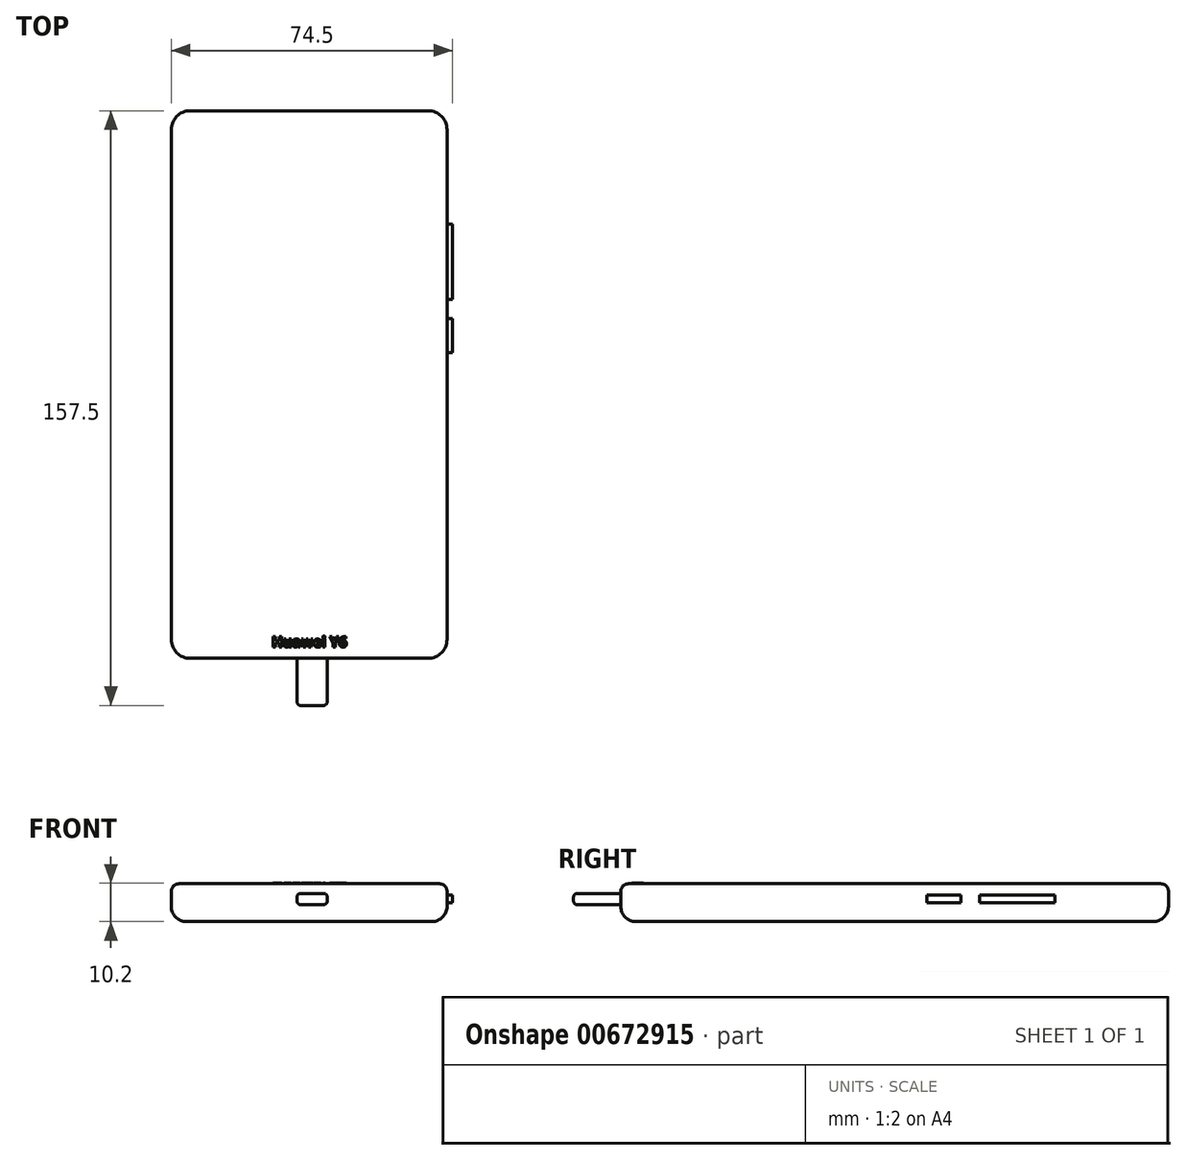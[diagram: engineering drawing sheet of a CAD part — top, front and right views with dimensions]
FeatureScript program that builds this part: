
annotation { "Feature Type Name" : "Feature", "Feature Type Description" : "" }
export const myFeature = defineFeature(function(context is Context, id is Id, definition is map)
    precondition{}
    {
        {
            var Q0;
            Q0=qCreatedBy(makeId("Top.planeOp"),FACE);
            var sketch = newSketch(context, id + "F0", { "sketchPlane" : qUnion([Q0])});
            skLineSegment(sketch, "E0.bottom", {"start": v(31.5, -72.5) * mm, "end": v(-31.5, -72.5) * mm});
            skLineSegment(sketch, "E0.top", {"start": v(31.5, 72.5) * mm, "end": v(-31.5, 72.5) * mm});
            skLineSegment(sketch, "E0.left", {"start": v(36.5, -67.5) * mm, "end": v(36.5, 67.5) * mm});
            skLineSegment(sketch, "E0.right", {"start": v(-36.5, -67.5) * mm, "end": v(-36.5, 67.5) * mm});
            skPoint(sketch, "E0.middle", {"position": v(0, 0) * mm});
            skPoint(sketch, "E1.visualSharp", {"position": v(-36.5, 72.5) * mm});
            skArc(sketch, "E1.filletArc", {"start": v(-31.5, 72.5) * mm, "mid": v(-35.04, 71.04) * mm, "end": v(-36.5, 67.5) * mm});
            skPoint(sketch, "E2.visualSharp", {"position": v(36.5, 72.5) * mm});
            skArc(sketch, "E2.filletArc", {"start": v(36.5, 67.5) * mm, "mid": v(35.04, 71.04) * mm, "end": v(31.5, 72.5) * mm});
            skPoint(sketch, "E3.visualSharp", {"position": v(36.5, -72.5) * mm});
            skArc(sketch, "E3.filletArc", {"start": v(31.5, -72.5) * mm, "mid": v(35.04, -71.04) * mm, "end": v(36.5, -67.5) * mm});
            skPoint(sketch, "E4.visualSharp", {"position": v(-36.5, -72.5) * mm});
            skArc(sketch, "E4.filletArc", {"start": v(-36.5, -67.5) * mm, "mid": v(-35.04, -71.04) * mm, "end": v(-31.5, -72.5) * mm});
            skSolve(sketch);
        }
        {
            var Q0;
            Q0 = qSketchRegion(id + "F0", true);
            extrude(context, id + "F1", {"entities" : qUnion([Q0]), "depth" : 10 * mm, "offsetDistance" : 25 * mm});
        }
        {
            var Q0;
            Q0=makeQuery(id+"F1.opExtrude","CAP_EDGE",EDGE,{"disambiguationData":[OSD([sQuery(id+"F0.wireOp",EDGE,"E1.filletArc")])],"isStart":false});
            fillet(context, id + "F2", {"entities" : qUnion([Q0]), "radius" : 2 * mm, "tangentPropagation" : true, "allowEdgeOverflow" : false});
        }
        {
            var Q0;
            Q0=makeQuery(id+"F1.opExtrude","CAP_EDGE",EDGE,{"disambiguationData":[OSD([sQuery(id+"F0.wireOp",EDGE,"E1.filletArc")])],"isStart":true});
            fillet(context, id + "F3", {"entities" : qUnion([Q0]), "radius" : 4 * mm, "tangentPropagation" : true, "allowEdgeOverflow" : false});
        }
        {
            var Q0;
            Q0=qCreatedBy(makeId("Right.planeOp"),FACE);
            var sketch = newSketch(context, id + "F4", { "sketchPlane" : qUnion([Q0])});
            skLineSegment(sketch, "E5.bottom", {"start": v(42.5, 7) * mm, "end": v(22.5, 7) * mm});
            skLineSegment(sketch, "E5.top", {"start": v(42.5, 5) * mm, "end": v(22.5, 5) * mm});
            skLineSegment(sketch, "E5.left", {"start": v(42.5, 7) * mm, "end": v(42.5, 5) * mm});
            skLineSegment(sketch, "E5.right", {"start": v(22.5, 7) * mm, "end": v(22.5, 5) * mm});
            skSolve(sketch);
        }
        {
            var Q0;
            Q0 = qSketchRegion(id + "F4", true);
            extrude(context, id + "F5", {"entities" : qUnion([Q0]), "operationType" : NewBodyOperationType.ADD, "depth" : 38 * mm, "offsetDistance" : 25 * mm});
        }
        {
            var Q0;
            Q0=qCreatedBy(makeId("Right.planeOp"),FACE);
            var sketch = newSketch(context, id + "F6", { "sketchPlane" : qUnion([Q0])});
            skLineSegment(sketch, "E6.bottom", {"start": v(8.5, 7) * mm, "end": v(17.5, 7) * mm});
            skLineSegment(sketch, "E6.top", {"start": v(8.5, 5) * mm, "end": v(17.5, 5) * mm});
            skLineSegment(sketch, "E6.left", {"start": v(8.5, 7) * mm, "end": v(8.5, 5) * mm});
            skLineSegment(sketch, "E6.right", {"start": v(17.5, 7) * mm, "end": v(17.5, 5) * mm});
            skSolve(sketch);
        }
        {
            var Q0;
            Q0 = qSketchRegion(id + "F6", true);
            extrude(context, id + "F7", {"entities" : qUnion([Q0]), "operationType" : NewBodyOperationType.ADD, "depth" : 38 * mm, "offsetDistance" : 25 * mm});
        }
        {
            var Q0;
            Q0=qCreatedBy(makeId("Front.planeOp"),FACE);
            var sketch = newSketch(context, id + "F8", { "sketchPlane" : qUnion([Q0])});
            skLineSegment(sketch, "E7.bottom", {"start": v(-3.21, 7.45) * mm, "end": v(4.79, 7.45) * mm});
            skLineSegment(sketch, "E7.top", {"start": v(-3.21, 4.45) * mm, "end": v(4.79, 4.45) * mm});
            skLineSegment(sketch, "E7.left", {"start": v(-3.21, 7.45) * mm, "end": v(-3.21, 4.45) * mm});
            skLineSegment(sketch, "E7.right", {"start": v(4.79, 7.45) * mm, "end": v(4.79, 4.45) * mm});
            skSolve(sketch);
        }
        {
            var Q0;
            Q0 = qSketchRegion(id + "F8", true);
            extrude(context, id + "F9", {"entities" : qUnion([Q0]), "operationType" : NewBodyOperationType.ADD, "depth" : 85 * mm, "offsetDistance" : 25 * mm});
        }
        {
            var Q0;
            Q0=makeQuery(id+"F9.opExtrude","SWEPT_EDGE",EDGE,{"disambiguationData":[OSD([sQuery(id+"F8.wireOp",EDGE,"E7.bottom"),sQuery(id+"F8.wireOp",EDGE,"E7.right")])]});
            var Q1;
            Q1=makeQuery(id+"F9.opExtrude","CAP_EDGE",EDGE,{"disambiguationData":[OSD([sQuery(id+"F8.wireOp",EDGE,"E7.bottom")])],"isStart":false});
            var Q2;
            Q2=makeQuery(id+"F9.opExtrude","SWEPT_EDGE",EDGE,{"disambiguationData":[OSD([sQuery(id+"F8.wireOp",EDGE,"E7.bottom"),sQuery(id+"F8.wireOp",EDGE,"E7.left")])]});
            var Q3;
            Q3=makeQuery(id+"F9.opExtrude","CAP_EDGE",EDGE,{"disambiguationData":[OSD([sQuery(id+"F8.wireOp",EDGE,"E7.left")])],"isStart":false});
            var Q4;
            Q4=makeQuery(id+"F9.opExtrude","SWEPT_EDGE",EDGE,{"disambiguationData":[OSD([sQuery(id+"F8.wireOp",EDGE,"E7.top"),sQuery(id+"F8.wireOp",EDGE,"E7.left")])]});
            var Q5;
            Q5=makeQuery(id+"F9.opExtrude","CAP_EDGE",EDGE,{"disambiguationData":[OSD([sQuery(id+"F8.wireOp",EDGE,"E7.top")])],"isStart":false});
            var Q6;
            Q6=makeQuery(id+"F9.opExtrude","SWEPT_EDGE",EDGE,{"disambiguationData":[OSD([sQuery(id+"F8.wireOp",EDGE,"E7.top"),sQuery(id+"F8.wireOp",EDGE,"E7.right")])]});
            var Q7;
            Q7=makeQuery(id+"F9.opExtrude","CAP_EDGE",EDGE,{"disambiguationData":[OSD([sQuery(id+"F8.wireOp",EDGE,"E7.right")])],"isStart":false});
            fillet(context, id + "F10", {"entities" : qUnion([Q0, Q1, Q2, Q3, Q4, Q5, Q6, Q7]), "radius" : 1 * mm, "tangentPropagation" : true, "allowEdgeOverflow" : false});
        }
        {
            var Q0;
            Q0=makeQuery(id+"F1.opExtrude","CAP_FACE",FACE,{"disambiguationData":[OSD([sQuery(id+"F0.wireOp",EDGE,"E0.bottom"),sQuery(id+"F0.wireOp",EDGE,"E0.top"),sQuery(id+"F0.wireOp",EDGE,"E0.left"),sQuery(id+"F0.wireOp",EDGE,"E0.right"),sQuery(id+"F0.wireOp",EDGE,"E1.filletArc"),sQuery(id+"F0.wireOp",EDGE,"E2.filletArc"),sQuery(id+"F0.wireOp",EDGE,"E3.filletArc"),sQuery(id+"F0.wireOp",EDGE,"E4.filletArc")])],"isStart":false});
            var sketch = newSketch(context, id + "F11", { "sketchPlane" : qUnion([Q0])});
            skText(sketch, "E8", { "text": "Huawei Y6", "fontName": "OpenSans-Bold.ttf"});
            const initialGuessF11  = {"E8": [-0.00985, -0.0695, 1, 0, 0.00273]};
            skSetInitialGuess(sketch, initialGuessF11);
            skSolve(sketch);
        }
        {
            var Q0;
            Q0 = qSketchRegion(id + "F11", true);
            extrude(context, id + "F12", {"entities" : qUnion([Q0]), "operationType" : NewBodyOperationType.ADD, "depth" : 0.2 * mm, "offsetDistance" : 25 * mm});
        }
    });
